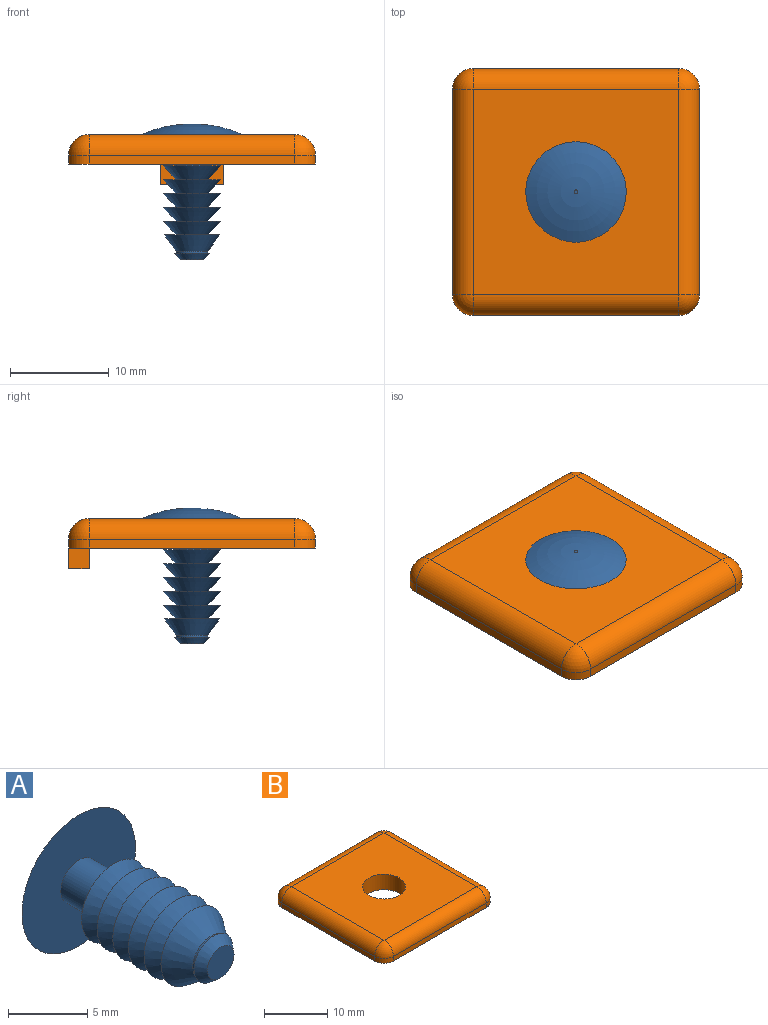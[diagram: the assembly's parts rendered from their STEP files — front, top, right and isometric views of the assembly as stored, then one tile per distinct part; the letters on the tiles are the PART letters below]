
ASSEMBLY  parts=2 mates=1
PART A: 31 faces, bbox 10.2x13.8x10.2 mm
  f0: plane 3.45x3.45mm, normal (0,1,0), area 1.3mm2, adj f1,f29
  f1: cylinder r=1.6mm len=12.04mm, axis (0,-1,0), area 67.6mm2, adj f0,f4,f5,f8,f9,f10,f11,f12
  f2: plane 0.4x0.4mm, normal (0,1,0), area 0.1mm2, adj f3
  f3: torus R=0.2mm, axis (0,-1,0), area 84.6mm2, adj f2,f4
  f4: plane 10.16x10.16mm, normal (0,-1,0), area 73mm2, adj f1,f3
  f5: cone r=2.8mm half-angle=36.1deg, axis (0,1,0), area 24.6mm2, adj f1,f6,f9,f11
  f6: plane 5.61x5.61mm, normal (0,1,0), area 14.5mm2, adj f5,f7,f9,f11
  f7: cone r=2.92mm half-angle=43.4deg, axis (0,1,0), area 23.8mm2, adj f6,f8,f10,f12
  f8: cone r=1.6mm half-angle=69deg, axis (0,1,0), area 17.5mm2, adj f1,f7,f10,f12
  f9: plane 1.65x0.87mm, normal (0.72,0,0.69), area 1mm2, adj f1,f5,f6
  f10: plane 1.4x0.95mm, normal (0.72,0,0.69), area 0.6mm2, adj f1,f7,f8
  f11: plane 1.65x1.2mm, normal (0,0,-1), area 1mm2, adj f1,f5,f6
  f12: plane 1.4x1.32mm, normal (0,0,-1), area 0.6mm2, adj f1,f7,f8
  f13: plane 1.4x0.95mm, normal (0.72,0,0.69), area 0.6mm2, adj f1,f15,f16
  f14: plane 1.4x1.32mm, normal (0,0,-1), area 0.6mm2, adj f1,f15,f16
  f15: cone r=2.92mm half-angle=43.4deg, axis (0,1,0), area 23.8mm2, adj f1,f13,f14,f16
  f16: cone r=1.6mm half-angle=69deg, axis (0,1,0), area 17.5mm2, adj f1,f13,f14,f15
  f17: plane 1.4x0.95mm, normal (0.72,0,0.69), area 0.6mm2, adj f1,f19,f20
  f18: plane 1.4x1.32mm, normal (0,0,-1), area 0.6mm2, adj f1,f19,f20
  f19: cone r=2.92mm half-angle=43.4deg, axis (0,1,0), area 23.8mm2, adj f1,f17,f18,f20
  f20: cone r=1.6mm half-angle=69deg, axis (0,1,0), area 17.5mm2, adj f1,f17,f18,f19
  f21: plane 1.4x0.95mm, normal (0.72,0,0.69), area 0.6mm2, adj f1,f23,f24
  f22: plane 1.4x1.32mm, normal (0,0,-1), area 0.6mm2, adj f1,f23,f24
  f23: cone r=2.92mm half-angle=43.4deg, axis (0,1,0), area 23.8mm2, adj f1,f21,f22,f24
  f24: cone r=1.6mm half-angle=69deg, axis (0,1,0), area 17.5mm2, adj f1,f21,f22,f23
  f25: plane 1.4x1.32mm, normal (0,0,-1), area 0.6mm2, adj f1,f27,f28
  f26: plane 1.4x0.95mm, normal (0.72,0,0.69), area 0.6mm2, adj f1,f27,f28
  f27: cone r=1.6mm half-angle=69deg, axis (0,1,0), area 17.5mm2, adj f1,f25,f26,f28
  f28: cone r=2.92mm half-angle=43.4deg, axis (0,1,0), area 23.8mm2, adj f1,f25,f26,f27
  f29: cone r=1.73mm half-angle=38.9deg, axis (0,1,0), area 7.8mm2, adj f0,f30
  f30: plane 2.39x2.39mm, normal (0,-1,0), area 4.5mm2, adj f29
PART B: 23 faces, bbox 25x25x5.1 mm
  f0: cylinder r=2.1mm len=20.8mm, axis (-1,0,0), area 68.6mm2, adj f2,f3,f14,f17
  f1: plane 25x25mm, normal (0,0,-1), area 571.7mm2, adj f2,f4,f6,f8,f10,f12,f13,f16
  f2: plane 20.8x3mm, normal (0,1,0), area 32mm2, adj f0,f1,f4,f13,f19,f21,f22
  f3: sphere r=2.1mm, area 6.9mm2, adj f0,f4,f5
  f4: cylinder r=2.1mm len=2.1mm, axis (0,0,-1), area 3mm2, adj f1,f2,f3,f6
  f5: cylinder r=2.1mm len=20.8mm, axis (0,1,0), area 68.6mm2, adj f3,f6,f7,f17
  f6: plane 20.8x0.9mm, normal (1,0,0), area 18.7mm2, adj f1,f4,f5,f8
  f7: sphere r=2.1mm, area 6.9mm2, adj f5,f8,f9
  f8: cylinder r=2.1mm len=2.1mm, axis (0,0,-1), area 3mm2, adj f1,f6,f7,f10
  f9: cylinder r=2.1mm len=20.8mm, axis (1,0,0), area 68.6mm2, adj f7,f10,f11,f17
  f10: plane 20.8x0.9mm, normal (0,-1,0), area 18.7mm2, adj f1,f8,f9,f12
  f11: sphere r=2.1mm, area 6.9mm2, adj f9,f12,f15
  f12: cylinder r=2.1mm len=2.1mm, axis (0,0,-1), area 3mm2, adj f1,f10,f11,f16
  f13: cylinder r=2.1mm len=2.1mm, axis (0,0,1), area 3mm2, adj f1,f2,f14,f16
  f14: sphere r=2.1mm, area 6.9mm2, adj f0,f13,f15
  f15: cylinder r=2.1mm len=20.8mm, axis (0,-1,0), area 68.6mm2, adj f11,f14,f16,f17
  f16: plane 20.8x0.9mm, normal (-1,0,0), area 18.7mm2, adj f1,f12,f13,f15
  f17: plane 20.8x20.8mm, normal (0,0,1), area 396.3mm2, adj f0,f5,f9,f15,f18
  f18: cylinder r=3.4mm len=6.8mm, axis (0,0,-1), area 64.1mm2, adj f1,f17
  f19: plane 2.1x2.1mm, normal (-1,0,0), area 4.4mm2, adj f1,f2,f20,f22
  f20: plane 6.3x2.1mm, normal (0,-1,0), area 13.2mm2, adj f1,f19,f21,f22
  f21: plane 2.1x2.1mm, normal (1,0,0), area 4.4mm2, adj f1,f2,f20,f22
  f22: plane 6.3x2.1mm, normal (0,0,-1), area 13.2mm2, adj f2,f19,f20,f21
PLACE A rot(axis=(1,0,0),90deg) t=(0,0,0)mm
PLACE B at identity fixed
MATE fastened B.f18 <-> A.f1  axis (0,0,1) through (0,0,0)mm
